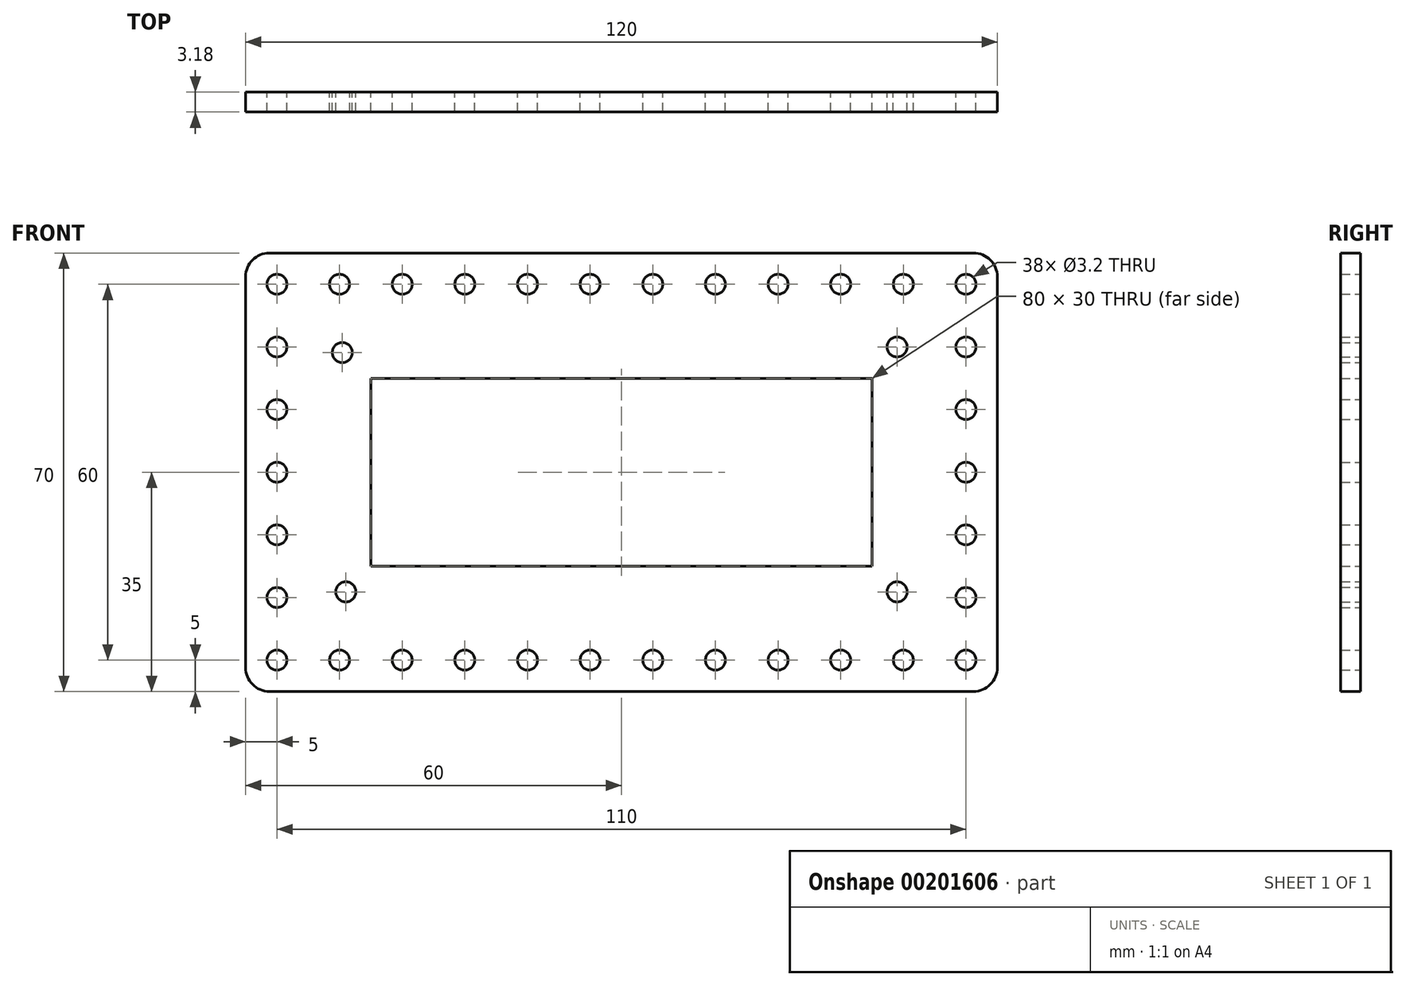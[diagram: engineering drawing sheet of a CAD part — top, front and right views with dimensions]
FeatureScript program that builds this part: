
annotation { "Feature Type Name" : "Feature", "Feature Type Description" : "" }
export const myFeature = defineFeature(function(context is Context, id is Id, definition is map)
    precondition{}
    {
        {
            var Q0;
            Q0=qCreatedBy(makeId("Front.planeOp"),FACE);
            var sketch = newSketch(context, id + "F0", { "sketchPlane" : qUnion([Q0])});
            skLineSegment(sketch, "E0.bottom", {"start": v(3.81, 0) * mm, "end": v(116.19, 0) * mm});
            skLineSegment(sketch, "E0.top", {"start": v(3.81, -70) * mm, "end": v(116.19, -70) * mm});
            skLineSegment(sketch, "E0.left", {"start": v(0, -3.81) * mm, "end": v(0, -66.19) * mm});
            skLineSegment(sketch, "E0.right", {"start": v(120, -3.81) * mm, "end": v(120, -66.19) * mm});
            skCircle(sketch, "E1", {"center": v(5, -5) * mm, "radius": 1.6 * mm});
            skCircle(sketch, "E2.1.0.0", {"center": v(15, -5) * mm, "radius": 1.6 * mm});
            skCircle(sketch, "E2.2.0.0", {"center": v(25, -5) * mm, "radius": 1.6 * mm});
            skCircle(sketch, "E2.3.0.0", {"center": v(35, -5) * mm, "radius": 1.6 * mm});
            skCircle(sketch, "E2.4.0.0", {"center": v(45, -5) * mm, "radius": 1.6 * mm});
            skCircle(sketch, "E2.5.0.0", {"center": v(55, -5) * mm, "radius": 1.6 * mm});
            skCircle(sketch, "E2.6.0.0", {"center": v(65, -5) * mm, "radius": 1.6 * mm});
            skCircle(sketch, "E2.7.0.0", {"center": v(75, -5) * mm, "radius": 1.6 * mm});
            skCircle(sketch, "E2.8.0.0", {"center": v(85, -5) * mm, "radius": 1.6 * mm});
            skCircle(sketch, "E2.9.0.0", {"center": v(95, -5) * mm, "radius": 1.6 * mm});
            skCircle(sketch, "E2.10.0.0", {"center": v(105, -5) * mm, "radius": 1.6 * mm});
            skCircle(sketch, "E2.11.0.0", {"center": v(115, -5) * mm, "radius": 1.6 * mm});
            skLineSegment(sketch, "E2.direction1", {"start": v(5, -5) * mm, "end": v(15, -5) * mm, "construction": true});
            skCircle(sketch, "E3.0.1.0", {"center": v(5, -15) * mm, "radius": 1.6 * mm});
            skCircle(sketch, "E3.0.2.0", {"center": v(5, -25) * mm, "radius": 1.6 * mm});
            skCircle(sketch, "E3.0.3.0", {"center": v(5, -35) * mm, "radius": 1.6 * mm});
            skCircle(sketch, "E3.0.4.0", {"center": v(5, -45) * mm, "radius": 1.6 * mm});
            skCircle(sketch, "E3.0.5.0", {"center": v(5, -55) * mm, "radius": 1.6 * mm});
            skCircle(sketch, "E3.0.6.0", {"center": v(5, -65) * mm, "radius": 1.6 * mm});
            skLineSegment(sketch, "E3.direction1", {"start": v(5, -5) * mm, "end": v(30.4, -5) * mm, "construction": true});
            skLineSegment(sketch, "E3.direction2", {"start": v(5, -5) * mm, "end": v(5, -15) * mm, "construction": true});
            skCircle(sketch, "E4.1.0.0", {"center": v(15, -65) * mm, "radius": 1.6 * mm});
            skCircle(sketch, "E4.2.0.0", {"center": v(25, -65) * mm, "radius": 1.6 * mm});
            skCircle(sketch, "E4.3.0.0", {"center": v(35, -65) * mm, "radius": 1.6 * mm});
            skCircle(sketch, "E4.4.0.0", {"center": v(45, -65) * mm, "radius": 1.6 * mm});
            skCircle(sketch, "E4.5.0.0", {"center": v(55, -65) * mm, "radius": 1.6 * mm});
            skCircle(sketch, "E4.6.0.0", {"center": v(65, -65) * mm, "radius": 1.6 * mm});
            skCircle(sketch, "E4.7.0.0", {"center": v(75, -65) * mm, "radius": 1.6 * mm});
            skCircle(sketch, "E4.8.0.0", {"center": v(85, -65) * mm, "radius": 1.6 * mm});
            skCircle(sketch, "E4.9.0.0", {"center": v(95, -65) * mm, "radius": 1.6 * mm});
            skCircle(sketch, "E4.10.0.0", {"center": v(105, -65) * mm, "radius": 1.6 * mm});
            skCircle(sketch, "E4.11.0.0", {"center": v(115, -65) * mm, "radius": 1.6 * mm});
            skLineSegment(sketch, "E4.direction1", {"start": v(5, -65) * mm, "end": v(15, -65) * mm, "construction": true});
            skCircle(sketch, "E5.0.1.0", {"center": v(115, -15) * mm, "radius": 1.6 * mm});
            skCircle(sketch, "E5.0.2.0", {"center": v(115, -25) * mm, "radius": 1.6 * mm});
            skCircle(sketch, "E5.0.3.0", {"center": v(115, -35) * mm, "radius": 1.6 * mm});
            skCircle(sketch, "E5.0.4.0", {"center": v(115, -45) * mm, "radius": 1.6 * mm});
            skCircle(sketch, "E5.0.5.0", {"center": v(115, -55) * mm, "radius": 1.6 * mm});
            skLineSegment(sketch, "E5.direction1", {"start": v(115, -5) * mm, "end": v(140.4, -5) * mm, "construction": true});
            skLineSegment(sketch, "E5.direction2", {"start": v(115, -5) * mm, "end": v(115, -15) * mm, "construction": true});
            skLineSegment(sketch, "E6.bottom", {"start": v(20, -20) * mm, "end": v(100, -20) * mm});
            skLineSegment(sketch, "E6.top", {"start": v(20, -50) * mm, "end": v(100, -50) * mm});
            skLineSegment(sketch, "E6.left", {"start": v(20, -20) * mm, "end": v(20, -50) * mm});
            skLineSegment(sketch, "E6.right", {"start": v(100, -20) * mm, "end": v(100, -50) * mm});
            skCircle(sketch, "E7", {"center": v(15.44, -15.9) * mm, "radius": 1.6 * mm});
            skCircle(sketch, "E8", {"center": v(104, -15) * mm, "radius": 1.6 * mm});
            skCircle(sketch, "E9", {"center": v(16, -54.1) * mm, "radius": 1.6 * mm});
            skCircle(sketch, "E10", {"center": v(104, -54.1) * mm, "radius": 1.6 * mm});
            skPoint(sketch, "E11.visualSharp", {"position": v(120, 0) * mm});
            skArc(sketch, "E11.filletArc", {"start": v(120, -3.81) * mm, "mid": v(118.88, -1.12) * mm, "end": v(116.19, 0) * mm});
            skPoint(sketch, "E12.visualSharp", {"position": v(120, -70) * mm});
            skArc(sketch, "E12.filletArc", {"start": v(116.19, -70) * mm, "mid": v(118.88, -68.88) * mm, "end": v(120, -66.19) * mm});
            skPoint(sketch, "E13.visualSharp", {"position": v(0, -70) * mm});
            skArc(sketch, "E13.filletArc", {"start": v(0, -66.19) * mm, "mid": v(1.12, -68.88) * mm, "end": v(3.81, -70) * mm});
            skPoint(sketch, "E14.visualSharp", {"position": v(0, 0) * mm});
            skArc(sketch, "E14.filletArc", {"start": v(3.81, 0) * mm, "mid": v(1.12, -1.12) * mm, "end": v(0, -3.81) * mm});
            skSolve(sketch);
        }
        {
            var Q0;
            Q0=makeQuery(id+"F0.imprint","IMPRINT",FACE,{"disambiguationData":[TD([[makeQuery(id+"F0.imprint","IMPRINT",EDGE,{"derivedFrom":sQuery(id+"F0.wireOp",EDGE,"E0.bottom")}),-1.0]])]});
            extrude(context, id + "F1", {"entities" : qUnion([Q0]), "depth" : 3.17 * mm});
        }
    });
